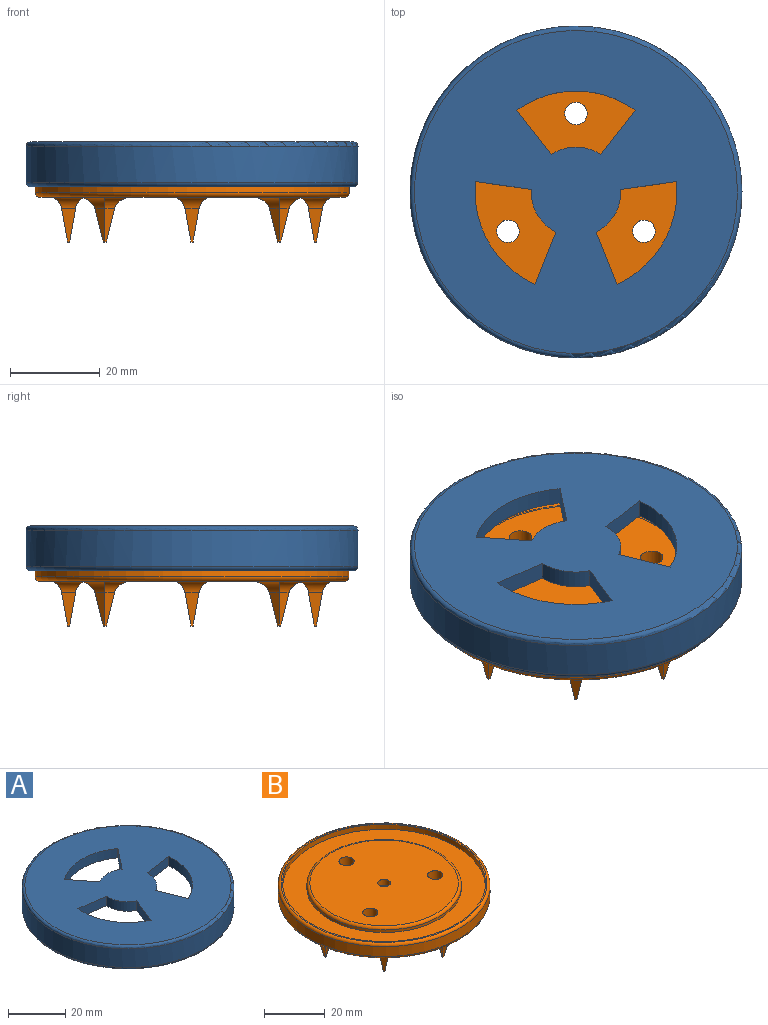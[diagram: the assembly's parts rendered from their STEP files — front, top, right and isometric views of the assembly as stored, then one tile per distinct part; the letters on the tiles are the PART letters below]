
ASSEMBLY  parts=2 mates=1
PART A: 19 faces, bbox 80.1x80.1x10 mm
  f0: plane 71x71mm, normal (0,0,-1), area 3212.1mm2, adj f3,f7,f8,f9,f10,f11,f12,f13
  f1: plane 72x72mm, normal (0,0,1), area 3324.4mm2, adj f6,f7,f8,f9,f10,f11,f12,f13
  f2: cylinder r=37mm len=74mm, axis (0,0,-1), area 1859.8mm2, adj f5,f6
  f3: cylinder r=35.5mm len=71mm, axis (0,0,1), area 1338.3mm2, adj f0,f4
  f4: plane 72x72mm, normal (0,0,-1), area 112.3mm2, adj f3,f5
  f5: torus R=36mm, axis (0,0,-1), area 361.6mm2, adj f2,f4
  f6: torus R=36mm, axis (0,0,1), area 361.6mm2, adj f1,f2
  f7: plane 12.4x4mm, normal (-0.14,-0.99,0), area 50.1mm2, adj f0,f1,f8,f10
  f8: cylinder r=10mm len=9.5mm, axis (0,0,-1), area 46.4mm2, adj f0,f1,f7,f9
  f9: plane 11.62x4.67mm, normal (-0.93,0.37,0), area 50.1mm2, adj f0,f1,f8,f10
  f10: cylinder r=22.5mm len=22.88mm, axis (0,0,-1), area 112.9mm2, adj f0,f1,f7,f9
  f11: plane 9.85x7.73mm, normal (-0.79,0.62,0), area 50.1mm2, adj f0,f1,f12,f14
  f12: cylinder r=10mm len=10.97mm, axis (0,0,-1), area 46.4mm2, adj f0,f1,f11,f13
  f13: plane 9.85x7.73mm, normal (0.79,0.62,0), area 50.1mm2, adj f0,f1,f12,f14
  f14: cylinder r=22.5mm len=26.42mm, axis (0,0,-1), area 112.9mm2, adj f0,f1,f11,f13
  f15: plane 11.62x4.67mm, normal (0.93,0.37,0), area 50.1mm2, adj f0,f1,f16,f18
  f16: cylinder r=10mm len=9.5mm, axis (0,0,-1), area 46.4mm2, adj f0,f1,f15,f17
  f17: plane 12.4x4mm, normal (0.14,-0.99,0), area 50.1mm2, adj f0,f1,f16,f18
  f18: cylinder r=22.5mm len=22.88mm, axis (0,0,-1), area 112.9mm2, adj f0,f1,f15,f17
PART B: 88 faces, bbox 75.8x75.8x16 mm
  f0: cylinder r=35mm len=70mm, axis (0,0,-1), area 879.6mm2, adj f86,f87
  f1: plane 68x68mm, normal (0,0,1), area 106mm2, adj f4,f87
  f2: plane 68x68mm, normal (0,0,-1), area 2857.7mm2, adj f47,f50,f51,f52,f53,f54,f55,f56
  f3: cylinder r=25.5mm len=51mm, axis (0,0,1), area 160.2mm2, adj f5,f85
  f4: cylinder r=33.5mm len=67mm, axis (0,0,1), area 421mm2, adj f1,f5
  f5: plane 67x67mm, normal (0,0,1), area 1482.8mm2, adj f3,f4
  f6: plane 49x49mm, normal (0,0,1), area 1813.5mm2, adj f49,f50,f51,f52,f85
  f7: plane 7.52x3.13mm, normal (0,-0.98,-0.17), area 13.7mm2, adj f8,f10,f11,f82
  f8: plane 7.52x3.13mm, normal (-0.98,0,-0.17), area 13.7mm2, adj f7,f9,f11,f84
  f9: plane 7.52x3.13mm, normal (0,0.98,-0.17), area 13.7mm2, adj f8,f10,f11,f83
  f10: plane 7.52x3.13mm, normal (0.98,0,-0.17), area 13.7mm2, adj f7,f9,f11,f81
  f11: plane 0.47x0.47mm, normal (0,0,-1), area 0.2mm2, adj f7,f8,f9,f10
  f12: plane 7.52x2.21mm, normal (-0.7,-0.7,-0.17), area 13.7mm2, adj f13,f15,f16,f77
  f13: plane 7.52x2.21mm, normal (-0.7,0.7,-0.17), area 13.7mm2, adj f12,f14,f16,f78
  f14: plane 7.52x2.21mm, normal (0.7,0.7,-0.17), area 13.7mm2, adj f13,f15,f16,f80
  f15: plane 7.52x2.21mm, normal (0.7,-0.7,-0.17), area 13.7mm2, adj f12,f14,f16,f79
  f16: plane 0.67x0.67mm, normal (0,0,-1), area 0.2mm2, adj f12,f13,f14,f15
  f17: plane 7.52x3.13mm, normal (-0.98,0,-0.17), area 13.7mm2, adj f18,f20,f21,f74
  f18: plane 7.52x3.13mm, normal (0,0.98,-0.17), area 13.7mm2, adj f17,f19,f21,f76
  f19: plane 7.52x3.13mm, normal (0.98,0,-0.17), area 13.7mm2, adj f18,f20,f21,f75
  f20: plane 7.52x3.13mm, normal (0,-0.98,-0.17), area 13.7mm2, adj f17,f19,f21,f73
  f21: plane 0.47x0.47mm, normal (0,0,-1), area 0.2mm2, adj f17,f18,f19,f20
  f22: plane 7.52x2.21mm, normal (-0.7,0.7,-0.17), area 13.7mm2, adj f23,f25,f26,f70
  f23: plane 7.52x2.21mm, normal (0.7,0.7,-0.17), area 13.7mm2, adj f22,f24,f26,f72
  f24: plane 7.52x2.21mm, normal (0.7,-0.7,-0.17), area 13.7mm2, adj f23,f25,f26,f71
  f25: plane 7.52x2.21mm, normal (-0.7,-0.7,-0.17), area 13.7mm2, adj f22,f24,f26,f69
  f26: plane 0.67x0.67mm, normal (0,0,-1), area 0.2mm2, adj f22,f23,f24,f25
  f27: plane 7.52x3.13mm, normal (0,0.98,-0.17), area 13.7mm2, adj f28,f30,f31,f66
  f28: plane 7.52x3.13mm, normal (0.98,0,-0.17), area 13.7mm2, adj f27,f29,f31,f68
  f29: plane 7.52x3.13mm, normal (0,-0.98,-0.17), area 13.7mm2, adj f28,f30,f31,f67
  f30: plane 7.52x3.13mm, normal (-0.98,0,-0.17), area 13.7mm2, adj f27,f29,f31,f65
  f31: plane 0.47x0.47mm, normal (0,0,-1), area 0.2mm2, adj f27,f28,f29,f30
  f32: plane 7.52x2.21mm, normal (0.7,0.7,-0.17), area 13.7mm2, adj f33,f35,f36,f62
  f33: plane 7.52x2.21mm, normal (0.7,-0.7,-0.17), area 13.7mm2, adj f32,f34,f36,f64
  f34: plane 7.52x2.21mm, normal (-0.7,-0.7,-0.17), area 13.7mm2, adj f33,f35,f36,f63
  f35: plane 7.52x2.21mm, normal (-0.7,0.7,-0.17), area 13.7mm2, adj f32,f34,f36,f61
  f36: plane 0.67x0.67mm, normal (0,0,-1), area 0.2mm2, adj f32,f33,f34,f35
  f37: plane 7.52x3.13mm, normal (0.98,0,-0.17), area 13.7mm2, adj f38,f40,f41,f58
  f38: plane 7.52x3.13mm, normal (0,-0.98,-0.17), area 13.7mm2, adj f37,f39,f41,f60
  f39: plane 7.52x3.13mm, normal (-0.98,0,-0.17), area 13.7mm2, adj f38,f40,f41,f59
  f40: plane 7.52x3.13mm, normal (0,0.98,-0.17), area 13.7mm2, adj f37,f39,f41,f57
  f41: plane 0.47x0.47mm, normal (0,0,-1), area 0.2mm2, adj f37,f38,f39,f40
  f42: plane 7.52x2.21mm, normal (0.7,-0.7,-0.17), area 13.7mm2, adj f43,f45,f46,f54
  f43: plane 7.52x2.21mm, normal (-0.7,-0.7,-0.17), area 13.7mm2, adj f42,f44,f46,f56
  f44: plane 7.52x2.21mm, normal (-0.7,0.7,-0.17), area 13.7mm2, adj f43,f45,f46,f55
  f45: plane 7.52x2.21mm, normal (0.7,0.7,-0.17), area 13.7mm2, adj f42,f44,f46,f53
  f46: plane 0.67x0.67mm, normal (0,0,-1), area 0.2mm2, adj f42,f43,f44,f45
  f47: cylinder r=4.45mm len=8.89mm, axis (0,0,-1), area 97.8mm2, adj f2,f48
  f48: plane 8.89x8.89mm, normal (0,0,-1), area 48.7mm2, adj f47,f49
  f49: cylinder r=2.06mm len=4.13mm, axis (0,0,-1), area 32.4mm2, adj f6,f48
  f50: cylinder r=2.5mm len=6mm, axis (0,0,1), area 94.2mm2, adj f2,f6
  f51: cylinder r=2.5mm len=6mm, axis (0,0,1), area 94.2mm2, adj f2,f6
  f52: cylinder r=2.5mm len=6mm, axis (0,0,1), area 94.2mm2, adj f2,f6
  f53: cylinder r=3mm len=8.48mm, axis (-0.71,0.71,0), area 23mm2, adj f2,f45,f54,f55
  f54: cylinder r=3mm len=8.48mm, axis (0.71,0.71,0), area 23mm2, adj f2,f42,f53,f56
  f55: cylinder r=3mm len=8.48mm, axis (0.71,0.71,0), area 23mm2, adj f2,f44,f53,f56
  f56: cylinder r=3mm len=8.48mm, axis (-0.71,0.71,0), area 23mm2, adj f2,f43,f54,f55
  f57: cylinder r=3mm len=9.03mm, axis (-1,0,0), area 23mm2, adj f2,f40,f58,f59
  f58: cylinder r=3mm len=9.03mm, axis (0,1,0), area 23mm2, adj f2,f37,f57,f60
  f59: cylinder r=3mm len=9.03mm, axis (0,1,0), area 23mm2, adj f2,f39,f57,f60
  f60: cylinder r=3mm len=9.03mm, axis (-1,0,0), area 23mm2, adj f2,f38,f58,f59
  f61: cylinder r=3mm len=8.48mm, axis (-0.71,-0.71,0), area 23mm2, adj f2,f35,f62,f63
  f62: cylinder r=3mm len=8.48mm, axis (-0.71,0.71,0), area 23mm2, adj f2,f32,f61,f64
  f63: cylinder r=3mm len=8.48mm, axis (-0.71,0.71,0), area 23mm2, adj f2,f34,f61,f64
  f64: cylinder r=3mm len=8.48mm, axis (-0.71,-0.71,0), area 23mm2, adj f2,f33,f62,f63
  f65: cylinder r=3mm len=9.03mm, axis (0,-1,0), area 23mm2, adj f2,f30,f66,f67
  f66: cylinder r=3mm len=9.03mm, axis (-1,0,0), area 23mm2, adj f2,f27,f65,f68
  f67: cylinder r=3mm len=9.03mm, axis (-1,0,0), area 23mm2, adj f2,f29,f65,f68
  f68: cylinder r=3mm len=9.03mm, axis (0,-1,0), area 23mm2, adj f2,f28,f66,f67
  f69: cylinder r=3mm len=8.48mm, axis (0.71,-0.71,0), area 23mm2, adj f2,f25,f70,f71
  f70: cylinder r=3mm len=8.48mm, axis (-0.71,-0.71,0), area 23mm2, adj f2,f22,f69,f72
  f71: cylinder r=3mm len=8.48mm, axis (-0.71,-0.71,0), area 23mm2, adj f2,f24,f69,f72
  f72: cylinder r=3mm len=8.48mm, axis (0.71,-0.71,0), area 23mm2, adj f2,f23,f70,f71
  f73: cylinder r=3mm len=9.03mm, axis (1,0,0), area 23mm2, adj f2,f20,f74,f75
  f74: cylinder r=3mm len=9.03mm, axis (0,-1,0), area 23mm2, adj f2,f17,f73,f76
  f75: cylinder r=3mm len=9.03mm, axis (0,-1,0), area 23mm2, adj f2,f19,f73,f76
  f76: cylinder r=3mm len=9.03mm, axis (1,0,0), area 23mm2, adj f2,f18,f74,f75
  f77: cylinder r=3mm len=8.48mm, axis (0.71,-0.71,0), area 23mm2, adj f2,f12,f78,f79
  f78: cylinder r=3mm len=8.48mm, axis (0.71,0.71,0), area 23mm2, adj f2,f13,f77,f80
  f79: cylinder r=3mm len=8.48mm, axis (0.71,0.71,0), area 23mm2, adj f2,f15,f77,f80
  f80: cylinder r=3mm len=8.48mm, axis (0.71,-0.71,0), area 23mm2, adj f2,f14,f78,f79
  f81: cylinder r=3mm len=9.03mm, axis (0,1,0), area 23mm2, adj f2,f10,f82,f83
  f82: cylinder r=3mm len=9.03mm, axis (1,0,0), area 23mm2, adj f2,f7,f81,f84
  f83: cylinder r=3mm len=9.03mm, axis (1,0,0), area 23mm2, adj f2,f9,f81,f84
  f84: cylinder r=3mm len=9.03mm, axis (0,1,0), area 23mm2, adj f2,f8,f82,f83
  f85: torus R=24.5mm, axis (0,0,1), area 248.1mm2, adj f3,f6
  f86: torus R=34mm, axis (0,0,1), area 341.8mm2, adj f0,f2
  f87: torus R=34mm, axis (0,0,1), area 341.8mm2, adj f0,f1
PLACE A t=(0,0,8.3)mm
PLACE B at identity
MATE cylindrical A.f3 <-> B.f0  axis (0,0,-1) through (0,0,2.3)mm
